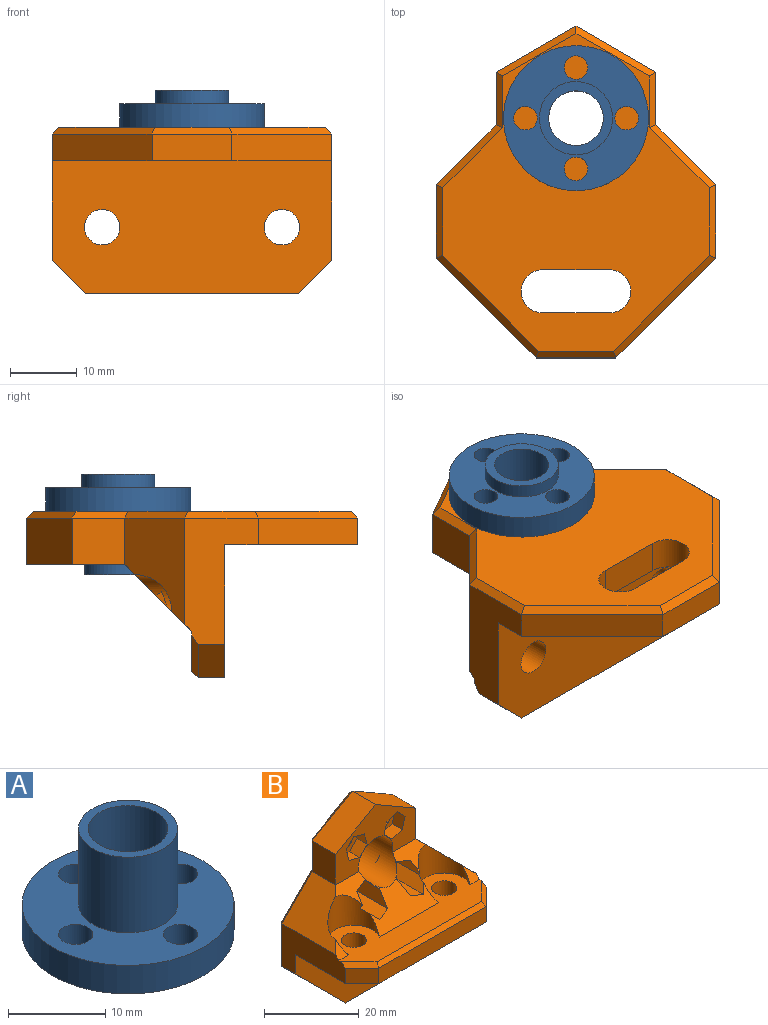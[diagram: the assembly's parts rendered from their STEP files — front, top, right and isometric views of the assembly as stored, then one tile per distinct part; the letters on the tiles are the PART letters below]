
ASSEMBLY  parts=2 mates=1
PART A: 12 faces, bbox 21.8x21.8x15.1 mm
  f0: cylinder r=1.77mm len=3.58mm, axis (0,0,-1), area 39.8mm2, adj f6,f7
  f1: cylinder r=1.77mm len=3.58mm, axis (0,0,-1), area 39.8mm2, adj f6,f7
  f2: cylinder r=1.77mm len=3.58mm, axis (0,0,-1), area 39.8mm2, adj f6,f7
  f3: cylinder r=1.77mm len=3.58mm, axis (0,0,-1), area 39.8mm2, adj f6,f7
  f4: cylinder r=4.1mm len=15.08mm, axis (0,0,-1), area 388.5mm2, adj f9,f11
  f5: cylinder r=10.89mm len=21.78mm, axis (0,0,-1), area 245mm2, adj f6,f7
  f6: plane 21.78x21.78mm, normal (0,0,1), area 252mm2, adj f0,f1,f2,f3,f5,f10
  f7: plane 21.78x21.78mm, normal (0,0,-1), area 238.2mm2, adj f0,f1,f2,f3,f5,f8
  f8: cylinder r=5.5mm len=11mm, axis (0,0,1), area 69.1mm2, adj f7,f9
  f9: plane 11x11mm, normal (0,0,-1), area 42.2mm2, adj f4,f8
  f10: cylinder r=5.08mm len=10.17mm, axis (0,0,-1), area 303.5mm2, adj f6,f11
  f11: plane 10.17x10.17mm, normal (0,0,1), area 28.4mm2, adj f4,f10
PART B: 77 faces, bbox 42x25x49.9 mm
  f0: plane 27x10mm, normal (0,-0.71,0.71), area 147.3mm2, adj f5,f6,f7,f12,f20,f29,f30,f35
  f1: cylinder r=1.65mm len=5mm, axis (0,-1,0), area 51.8mm2, adj f14,f49
  f2: cylinder r=1.65mm len=5mm, axis (0,-1,0), area 51.8mm2, adj f14,f56
  f3: cylinder r=1.65mm len=5mm, axis (0,-1,0), area 51.8mm2, adj f14,f39
  f4: cylinder r=1.65mm len=5mm, axis (0,-1,0), area 51.8mm2, adj f14,f46
  f5: plane 24x14.86mm, normal (0,-1,0), area 167.2mm2, adj f0,f20,f25,f26,f27,f28,f50,f51
  f6: cylinder r=5.5mm len=11mm, axis (0,0,-1), area 107.3mm2, adj f0,f11,f12,f30,f47,f48
  f7: cylinder r=5.5mm len=11mm, axis (0,0,-1), area 107.3mm2, adj f0,f10,f12,f29,f40,f41
  f8: cylinder r=2.65mm len=5.3mm, axis (0,0,-1), area 83.3mm2, adj f12,f16
  f9: cylinder r=2.65mm len=5.3mm, axis (0,0,-1), area 83.3mm2, adj f12,f16
  f10: plane 3x3mm, normal (0,-0.71,0.71), area 6.9mm2, adj f7,f12,f18,f29
  f11: plane 3x3mm, normal (0,-0.71,0.71), area 6.9mm2, adj f6,f12,f17,f30
  f12: plane 42x14.5mm, normal (0,0,1), area 336.2mm2, adj f0,f6,f7,f8,f9,f10,f11,f17
  f13: plane 42x20mm, normal (0,-1,0), area 516.8mm2, adj f16,f17,f18,f19,f21,f22,f23,f24
  f14: plane 47.7x40mm, normal (0,1,0), area 1079.6mm2, adj f1,f2,f3,f4,f20,f21,f22,f23
  f15: plane 32x4mm, normal (0,-1,0), area 128mm2, adj f16,f31,f32,f64
  f16: plane 42x20mm, normal (0,0,-1), area 770.9mm2, adj f8,f9,f13,f15,f17,f18,f31,f32
  f17: plane 19x11mm, normal (1,0,0), area 130.8mm2, adj f11,f12,f13,f16,f30,f31,f34,f65
  f18: plane 19x11mm, normal (-1,0,0), area 130.8mm2, adj f10,f12,f13,f16,f29,f32,f33,f63
  f19: plane 12x4mm, normal (0,0,-1), area 48mm2, adj f13,f33,f34,f71
  f20: cylinder r=5.15mm len=12.16mm, axis (0,-1,0), area 296.7mm2, adj f0,f5,f14
  f21: cylinder r=3.25mm len=6.5mm, axis (0,1,0), area 51.1mm2, adj f13,f14,f22,f23
  f22: plane 10x5mm, normal (0,0,-1), area 50mm2, adj f13,f14,f21,f24
  f23: plane 10x5mm, normal (0,0,1), area 50mm2, adj f13,f14,f21,f24
  f24: cylinder r=3.25mm len=6.5mm, axis (0,1,0), area 51.1mm2, adj f13,f14,f22,f23
  f25: plane 7.93x7mm, normal (1,0,0), area 55.5mm2, adj f5,f26,f30,f74
  f26: plane 12x7mm, normal (0.5,0,0.87), area 97mm2, adj f5,f25,f27,f72
  f27: plane 12x7mm, normal (-0.5,0,0.87), area 97mm2, adj f5,f26,f28,f70
  f28: plane 7.93x7mm, normal (-1,0,0), area 55.5mm2, adj f5,f27,f29,f68
  f29: plane 16x9mm, normal (-0.71,0,0.71), area 134.2mm2, adj f0,f7,f10,f18,f28,f66
  f30: plane 16x9mm, normal (0.71,0,0.71), area 134.2mm2, adj f0,f6,f11,f17,f25,f76
  f31: plane 5x5mm, normal (0.71,-0.71,0), area 28.3mm2, adj f15,f16,f17,f65
  f32: plane 5x5mm, normal (-0.71,-0.71,0), area 28.3mm2, adj f15,f16,f18,f63
  f33: plane 15x15mm, normal (-0.71,0,-0.71), area 84.9mm2, adj f13,f18,f19,f69
  f34: plane 15x15mm, normal (0.71,0,-0.71), area 84.9mm2, adj f13,f17,f19,f73
  f35: plane 10.78x3.12mm, normal (-0.26,0,0.97), area 33.5mm2, adj f0,f36,f39,f41
  f36: plane 9.94x3.12mm, normal (-0.97,0,0.26), area 27.1mm2, adj f0,f35,f37,f39
  f37: plane 6.82x2.29mm, normal (-0.71,0,-0.71), area 18.4mm2, adj f0,f36,f38,f39
  f38: plane 5.37x3.12mm, normal (0.26,0,-0.97), area 16mm2, adj f0,f37,f39,f40
  f39: plane 6.25x6.25mm, normal (0,-1,0), area 18.6mm2, adj f3,f35,f36,f37,f38,f40,f41
  f40: plane 7.61x3.12mm, normal (0.97,0,-0.26), area 21.8mm2, adj f0,f7,f38,f39,f41
  f41: plane 10.78x2.29mm, normal (0.71,0,0.71), area 30.3mm2, adj f0,f7,f35,f39,f40
  f42: plane 5.37x3.12mm, normal (-0.26,0,-0.97), area 16mm2, adj f0,f43,f46,f47
  f43: plane 6.82x2.29mm, normal (0.71,0,-0.71), area 18.4mm2, adj f0,f42,f44,f46
  f44: plane 9.94x3.12mm, normal (0.97,0,0.26), area 27.1mm2, adj f0,f43,f45,f46
  f45: plane 10.78x3.12mm, normal (0.26,0,0.97), area 33.5mm2, adj f0,f44,f46,f48
  f46: plane 6.25x6.25mm, normal (0,-1,0), area 18.6mm2, adj f4,f42,f43,f44,f45,f47,f48
  f47: plane 7.61x3.12mm, normal (-0.97,0,-0.26), area 21.8mm2, adj f0,f6,f42,f46,f48
  f48: plane 10.78x2.29mm, normal (-0.71,0,0.71), area 30.3mm2, adj f0,f6,f45,f46,f47
  f49: plane 6.25x6.25mm, normal (0,-1,0), area 18.6mm2, adj f1,f50,f51,f52,f53,f54,f55
  f50: plane 3.12x3mm, normal (-0.97,0,0.26), area 9.7mm2, adj f5,f49,f51,f55
  f51: plane 3x2.29mm, normal (-0.71,0,-0.71), area 9.7mm2, adj f5,f49,f50,f52
  f52: plane 3.12x3mm, normal (0.26,0,-0.97), area 9.7mm2, adj f5,f49,f51,f53
  f53: plane 3.12x3mm, normal (0.97,0,-0.26), area 9.7mm2, adj f5,f49,f52,f54
  f54: plane 3x2.29mm, normal (0.71,0,0.71), area 9.7mm2, adj f5,f49,f53,f55
  f55: plane 3.12x3mm, normal (-0.26,0,0.97), area 9.7mm2, adj f5,f49,f50,f54
  f56: plane 6.25x6.25mm, normal (0,-1,0), area 18.6mm2, adj f2,f57,f58,f59,f60,f61,f62
  f57: plane 3.12x3mm, normal (0.97,0,0.26), area 9.7mm2, adj f5,f56,f58,f62
  f58: plane 3.12x3mm, normal (0.26,0,0.97), area 9.7mm2, adj f5,f56,f57,f59
  f59: plane 3x2.29mm, normal (-0.71,0,0.71), area 9.7mm2, adj f5,f56,f58,f60
  f60: plane 3.12x3mm, normal (-0.97,0,-0.26), area 9.7mm2, adj f5,f56,f59,f61
  f61: plane 3.12x3mm, normal (-0.26,0,-0.97), area 9.7mm2, adj f5,f56,f60,f62
  f62: plane 3x2.29mm, normal (0.71,0,-0.71), area 9.7mm2, adj f5,f56,f57,f61
  f63: plane 6.41x5.41mm, normal (-0.5,-0.5,0.71), area 10.4mm2, adj f12,f18,f32,f64
  f64: plane 32x1mm, normal (0,-0.71,0.71), area 44.7mm2, adj f12,f15,f63,f65
  f65: plane 6.41x5.41mm, normal (0.5,-0.5,0.71), area 10.4mm2, adj f12,f17,f31,f64
  f66: plane 10x9.41mm, normal (-0.5,0.71,0.5), area 18mm2, adj f14,f29,f67,f68
  f67: plane 11x1mm, normal (-0.71,0.71,0), area 15mm2, adj f14,f18,f66,f69
  f68: plane 8.34x1mm, normal (-0.71,0.71,0), area 11.1mm2, adj f14,f28,f66,f70
  f69: plane 15.41x15.41mm, normal (-0.5,0.71,-0.5), area 29.4mm2, adj f14,f33,f67,f71
  f70: plane 12x7.51mm, normal (-0.35,0.71,0.61), area 18.8mm2, adj f14,f27,f68,f72
  f71: plane 12x1mm, normal (0,0.71,-0.71), area 16.4mm2, adj f14,f19,f69,f73
  f72: plane 12x7.51mm, normal (0.35,0.71,0.61), area 18.8mm2, adj f14,f26,f70,f74
  f73: plane 15.41x15.41mm, normal (0.5,0.71,-0.5), area 29.4mm2, adj f14,f34,f71,f75
  f74: plane 8.34x1mm, normal (0.71,0.71,0), area 11.1mm2, adj f14,f25,f72,f76
  f75: plane 11x1mm, normal (0.71,0.71,0), area 15mm2, adj f14,f17,f73,f76
  f76: plane 10x9.41mm, normal (0.5,0.71,0.5), area 18mm2, adj f14,f30,f74,f75
PLACE A rot(axis=(1,0,0),180deg) t=(-0.93,40.12,-108.01)mm
PLACE B rot(axis=(0,-0.71,-0.71),180deg) t=(-0.93,33.12,-111.59)mm
MATE fastened A.f8 <-> B.f20  axis (0,0,-1) through (-0.93,40.12,-111.59)mm
